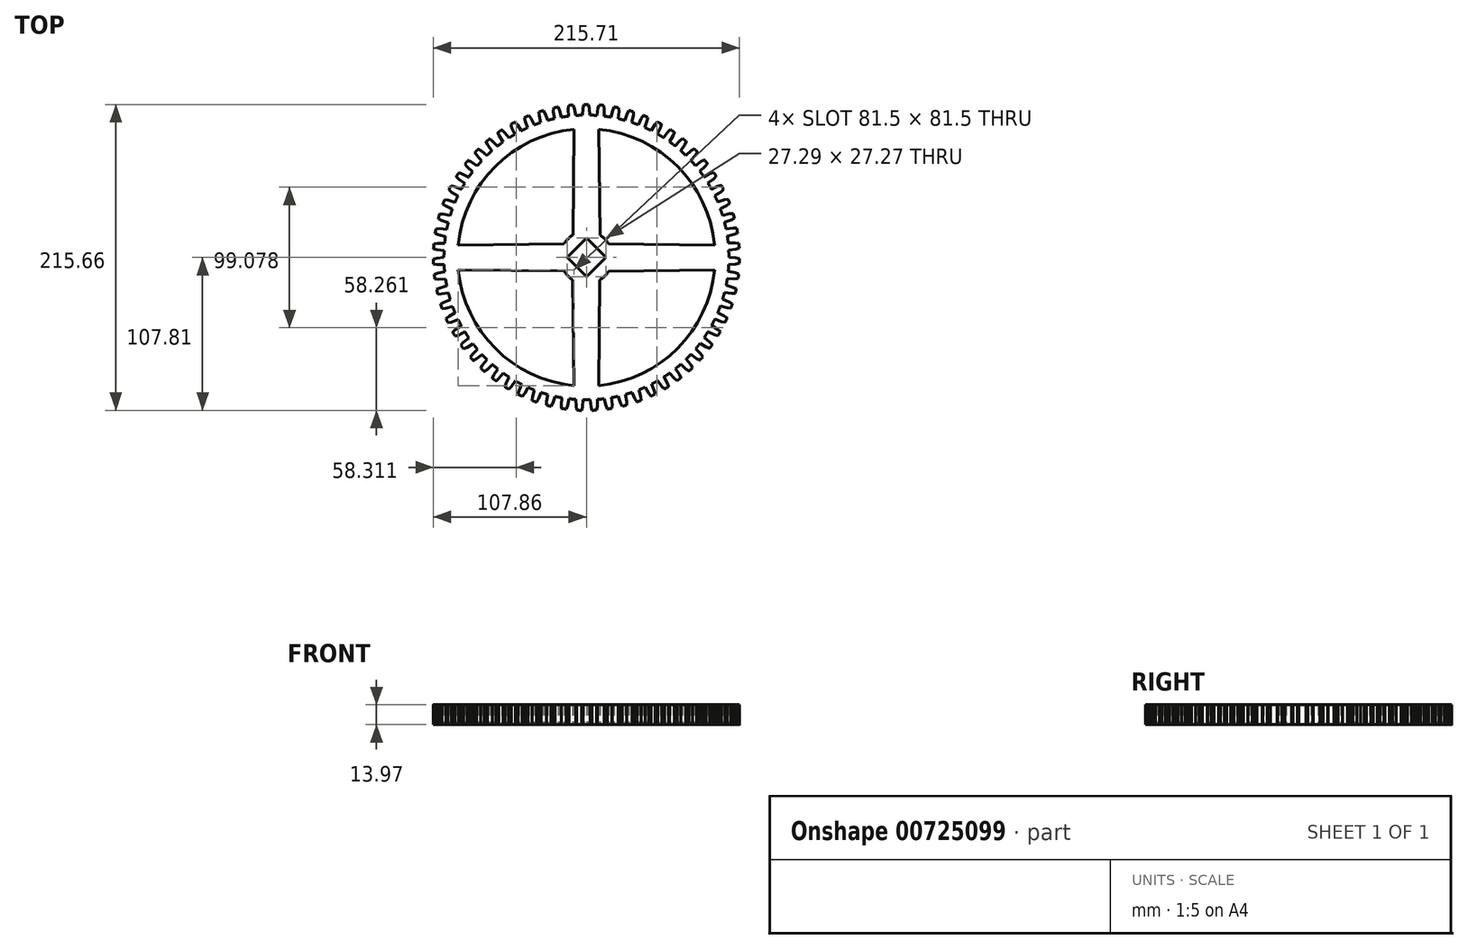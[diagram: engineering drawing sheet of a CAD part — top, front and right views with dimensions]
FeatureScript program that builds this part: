
annotation { "Feature Type Name" : "Feature", "Feature Type Description" : "" }
export const myFeature = defineFeature(function(context is Context, id is Id, definition is map)
    precondition{}
    {
        {
            var Q0;
            Q0=qCreatedBy(makeId("Top.planeOp"),FACE);
            var sketch = newSketch(context, id + "F0", { "sketchPlane" : qUnion([Q0])});
            skCircle(sketch, "E0", {"center": v(0, 0) * mm, "radius": 90.72 * mm});
            skCircle(sketch, "E1", {"center": v(0, 0) * mm, "radius": 107.86 * mm});
            skCircle(sketch, "E2", {"center": v(0, 0) * mm, "radius": 18.41 * mm});
            skLineSegment(sketch, "E3", {"start": v(0, 18.41) * mm, "end": v(0, 90.72) * mm});
            skLineSegment(sketch, "E4", {"start": v(18.41, 0) * mm, "end": v(90.72, 0) * mm});
            skLineSegment(sketch, "E5", {"start": v(-18.41, 0) * mm, "end": v(-90.72, 0) * mm});
            skLineSegment(sketch, "E6", {"start": v(0, -18.41) * mm, "end": v(0, -90.72) * mm});
            skLineSegment(sketch, "E7", {"start": v(9.72, 15.64) * mm, "end": v(8.79, 90.29) * mm});
            skLineSegment(sketch, "E8", {"start": v(-9.49, 15.78) * mm, "end": v(-8.79, 90.29) * mm});
            skLineSegment(sketch, "E9.1.0", {"start": v(-15.64, 9.72) * mm, "end": v(-90.29, 8.79) * mm});
            skLineSegment(sketch, "E9.1.1", {"start": v(-15.78, -9.49) * mm, "end": v(-90.29, -8.79) * mm});
            skLineSegment(sketch, "E9.2.0", {"start": v(-9.72, -15.64) * mm, "end": v(-8.79, -90.29) * mm});
            skLineSegment(sketch, "E9.2.1", {"start": v(9.49, -15.78) * mm, "end": v(8.79, -90.29) * mm});
            skLineSegment(sketch, "E9.3.0", {"start": v(15.64, -9.72) * mm, "end": v(90.29, -8.79) * mm});
            skLineSegment(sketch, "E9.3.1", {"start": v(15.78, 9.49) * mm, "end": v(90.29, 8.79) * mm});
            skLineSegment(sketch, "E10", {"start": v(0, 0) * mm, "end": v(0, -13.63) * mm});
            skLineSegment(sketch, "E11.bottom", {"start": v(127.17, 43.61) * mm, "end": v(146.45, 43.61) * mm});
            skLineSegment(sketch, "E11.top", {"start": v(127.17, 24.34) * mm, "end": v(146.45, 24.34) * mm});
            skLineSegment(sketch, "E11.left", {"start": v(127.17, 43.61) * mm, "end": v(127.17, 24.34) * mm});
            skLineSegment(sketch, "E11.right", {"start": v(146.45, 43.61) * mm, "end": v(146.45, 24.34) * mm});
            skLineSegment(sketch, "E12", {"start": v(0, -13.63) * mm, "end": v(-13.64, 0) * mm});
            skLineSegment(sketch, "E13", {"start": v(-13.64, 0) * mm, "end": v(0, 13.65) * mm});
            skLineSegment(sketch, "E14", {"start": v(0, 13.65) * mm, "end": v(13.66, 0) * mm});
            skLineSegment(sketch, "E15", {"start": v(13.66, 0) * mm, "end": v(0, -13.63) * mm});
            skLineSegment(sketch, "E16", {"start": v(0, 90.72) * mm, "end": v(-0.21, 107.86) * mm});
            skArc(sketch, "E17", {"start": v(-79.91, -60.73) * mm, "mid": v(84.25, 54.55) * mm, "end": v(-88.1, -48.07) * mm});
            skLineSegment(sketch, "E18", {"start": v(-0.18, 105.32) * mm, "end": v(-1.03, 105.31) * mm});
            skLineSegment(sketch, "E19", {"start": v(-0.18, 105.32) * mm, "end": v(2.05, 105.32) * mm});
            skLineSegment(sketch, "E20", {"start": v(2.42, 100.34) * mm, "end": v(2.05, 105.32) * mm});
            skLineSegment(sketch, "E21", {"start": v(1.44, 107.85) * mm, "end": v(2.05, 105.32) * mm});
            skLineSegment(sketch, "E22", {"start": v(-0.18, 105.32) * mm, "end": v(-2.42, 105.32) * mm});
            skLineSegment(sketch, "E23", {"start": v(-2.66, 100.33) * mm, "end": v(-2.42, 105.32) * mm});
            skLineSegment(sketch, "E24", {"start": v(-1.86, 107.84) * mm, "end": v(-2.42, 105.32) * mm});
            skLineSegment(sketch, "E25.1.0", {"start": v(-12.6, 107.12) * mm, "end": v(-12.9, 104.56) * mm});
            skLineSegment(sketch, "E25.1.1", {"start": v(-12.64, 99.57) * mm, "end": v(-12.9, 104.56) * mm});
            skLineSegment(sketch, "E25.1.2", {"start": v(-9.3, 107.46) * mm, "end": v(-8.44, 105) * mm});
            skLineSegment(sketch, "E25.1.3", {"start": v(-7.58, 100.08) * mm, "end": v(-8.44, 105) * mm});
            skLineSegment(sketch, "E25.2.0", {"start": v(-23.2, 105.34) * mm, "end": v(-23.24, 102.75) * mm});
            skLineSegment(sketch, "E25.2.1", {"start": v(-22.49, 97.82) * mm, "end": v(-23.24, 102.75) * mm});
            skLineSegment(sketch, "E25.2.2", {"start": v(-19.96, 106) * mm, "end": v(-18.86, 103.64) * mm});
            skLineSegment(sketch, "E25.2.3", {"start": v(-17.5, 98.83) * mm, "end": v(-18.86, 103.64) * mm});
            skLineSegment(sketch, "E25.3.0", {"start": v(-33.57, 102.5) * mm, "end": v(-33.35, 99.93) * mm});
            skLineSegment(sketch, "E25.3.1", {"start": v(-32.12, 95.1) * mm, "end": v(-33.35, 99.93) * mm});
            skLineSegment(sketch, "E25.3.2", {"start": v(-30.42, 103.48) * mm, "end": v(-29.08, 101.25) * mm});
            skLineSegment(sketch, "E25.3.3", {"start": v(-27.26, 96.6) * mm, "end": v(-29.08, 101.25) * mm});
            skLineSegment(sketch, "E25.4.0", {"start": v(-43.6, 98.65) * mm, "end": v(-43.14, 96.11) * mm});
            skLineSegment(sketch, "E25.4.1", {"start": v(-41.42, 91.42) * mm, "end": v(-43.14, 96.11) * mm});
            skLineSegment(sketch, "E25.4.2", {"start": v(-40.57, 99.94) * mm, "end": v(-39.02, 97.85) * mm});
            skLineSegment(sketch, "E25.4.3", {"start": v(-36.74, 93.4) * mm, "end": v(-39.02, 97.85) * mm});
            skLineSegment(sketch, "E25.5.0", {"start": v(-53.21, 93.82) * mm, "end": v(-52.5, 91.34) * mm});
            skLineSegment(sketch, "E25.5.1", {"start": v(-50.32, 86.84) * mm, "end": v(-52.5, 91.34) * mm});
            skLineSegment(sketch, "E25.5.2", {"start": v(-50.32, 95.4) * mm, "end": v(-48.57, 93.48) * mm});
            skLineSegment(sketch, "E25.5.3", {"start": v(-45.86, 89.28) * mm, "end": v(-48.57, 93.48) * mm});
            skLineSegment(sketch, "E25.6.0", {"start": v(-62.3, 88.06) * mm, "end": v(-61.33, 85.66) * mm});
            skLineSegment(sketch, "E25.6.1", {"start": v(-58.72, 81.4) * mm, "end": v(-61.33, 85.66) * mm});
            skLineSegment(sketch, "E25.6.2", {"start": v(-59.57, 89.92) * mm, "end": v(-57.63, 88.18) * mm});
            skLineSegment(sketch, "E25.6.3", {"start": v(-54.52, 84.27) * mm, "end": v(-57.63, 88.18) * mm});
            skLineSegment(sketch, "E25.7.0", {"start": v(-70.75, 81.42) * mm, "end": v(-69.55, 79.13) * mm});
            skLineSegment(sketch, "E25.7.1", {"start": v(-66.53, 75.15) * mm, "end": v(-69.55, 79.13) * mm});
            skLineSegment(sketch, "E25.7.2", {"start": v(-68.22, 83.54) * mm, "end": v(-66.13, 82) * mm});
            skLineSegment(sketch, "E25.7.3", {"start": v(-62.64, 78.42) * mm, "end": v(-66.13, 82) * mm});
            skLineSegment(sketch, "E25.8.0", {"start": v(-78.5, 73.97) * mm, "end": v(-77.08, 71.8) * mm});
            skLineSegment(sketch, "E25.8.1", {"start": v(-73.68, 68.15) * mm, "end": v(-77.08, 71.8) * mm});
            skLineSegment(sketch, "E25.8.2", {"start": v(-76.2, 76.34) * mm, "end": v(-73.96, 75) * mm});
            skLineSegment(sketch, "E25.8.3", {"start": v(-70.14, 71.8) * mm, "end": v(-73.96, 75) * mm});
            skLineSegment(sketch, "E25.9.0", {"start": v(-85.48, 65.78) * mm, "end": v(-83.85, 63.78) * mm});
            skLineSegment(sketch, "E25.9.1", {"start": v(-80.1, 60.48) * mm, "end": v(-83.85, 63.78) * mm});
            skLineSegment(sketch, "E25.9.2", {"start": v(-83.42, 68.37) * mm, "end": v(-81.06, 67.27) * mm});
            skLineSegment(sketch, "E25.9.3", {"start": v(-76.94, 64.45) * mm, "end": v(-81.06, 67.27) * mm});
            skLineSegment(sketch, "E25.10.0", {"start": v(-91.6, 56.95) * mm, "end": v(-89.78, 55.11) * mm});
            skLineSegment(sketch, "E25.10.1", {"start": v(-85.73, 52.2) * mm, "end": v(-89.78, 55.11) * mm});
            skLineSegment(sketch, "E25.10.2", {"start": v(-89.82, 59.72) * mm, "end": v(-87.36, 58.87) * mm});
            skLineSegment(sketch, "E25.10.3", {"start": v(-82.97, 56.47) * mm, "end": v(-87.36, 58.87) * mm});
            skLineSegment(sketch, "E25.11.0", {"start": v(-96.82, 47.54) * mm, "end": v(-94.82, 45.9) * mm});
            skLineSegment(sketch, "E25.11.1", {"start": v(-90.5, 43.4) * mm, "end": v(-94.82, 45.9) * mm});
            skLineSegment(sketch, "E25.11.2", {"start": v(-95.32, 50.48) * mm, "end": v(-92.79, 49.88) * mm});
            skLineSegment(sketch, "E25.11.3", {"start": v(-88.18, 47.93) * mm, "end": v(-92.79, 49.88) * mm});
            skLineSegment(sketch, "E25.12.0", {"start": v(-101.07, 37.67) * mm, "end": v(-98.92, 36.23) * mm});
            skLineSegment(sketch, "E25.12.1", {"start": v(-94.37, 34.18) * mm, "end": v(-98.92, 36.23) * mm});
            skLineSegment(sketch, "E25.12.2", {"start": v(-99.87, 40.74) * mm, "end": v(-97.3, 40.4) * mm});
            skLineSegment(sketch, "E25.12.3", {"start": v(-92.52, 38.91) * mm, "end": v(-97.3, 40.4) * mm});
            skLineSegment(sketch, "E25.13.0", {"start": v(-104.32, 27.41) * mm, "end": v(-102.04, 26.2) * mm});
            skLineSegment(sketch, "E25.13.1", {"start": v(-97.3, 24.61) * mm, "end": v(-102.04, 26.2) * mm});
            skLineSegment(sketch, "E25.13.2", {"start": v(-103.43, 30.6) * mm, "end": v(-100.83, 30.5) * mm});
            skLineSegment(sketch, "E25.13.3", {"start": v(-95.93, 29.5) * mm, "end": v(-100.83, 30.5) * mm});
            skLineSegment(sketch, "E25.14.0", {"start": v(-106.53, 16.9) * mm, "end": v(-104.14, 15.9) * mm});
            skLineSegment(sketch, "E25.14.1", {"start": v(-99.27, 14.8) * mm, "end": v(-104.14, 15.9) * mm});
            skLineSegment(sketch, "E25.14.2", {"start": v(-105.96, 20.14) * mm, "end": v(-103.36, 20.31) * mm});
            skLineSegment(sketch, "E25.14.3", {"start": v(-98.4, 19.8) * mm, "end": v(-103.36, 20.31) * mm});
            skLineSegment(sketch, "E25.15.0", {"start": v(-107.68, 6.2) * mm, "end": v(-105.2, 5.46) * mm});
            skLineSegment(sketch, "E25.15.1", {"start": v(-100.25, 4.85) * mm, "end": v(-105.2, 5.46) * mm});
            skLineSegment(sketch, "E25.15.2", {"start": v(-107.44, 9.5) * mm, "end": v(-104.87, 9.92) * mm});
            skLineSegment(sketch, "E25.15.3", {"start": v(-99.88, 9.91) * mm, "end": v(-104.87, 9.92) * mm});
            skLineSegment(sketch, "E25.16.0", {"start": v(-107.77, -4.55) * mm, "end": v(-105.23, -5.04) * mm});
            skLineSegment(sketch, "E25.16.1", {"start": v(-100.24, -5.16) * mm, "end": v(-105.23, -5.04) * mm});
            skLineSegment(sketch, "E25.16.2", {"start": v(-107.85, -1.25) * mm, "end": v(-105.34, -0.57) * mm});
            skLineSegment(sketch, "E25.16.3", {"start": v(-100.37, -0.08) * mm, "end": v(-105.34, -0.57) * mm});
            skLineSegment(sketch, "E25.17.0", {"start": v(-106.78, -15.26) * mm, "end": v(-104.2, -15.5) * mm});
            skLineSegment(sketch, "E25.17.1", {"start": v(-99.22, -15.11) * mm, "end": v(-104.2, -15.5) * mm});
            skLineSegment(sketch, "E25.17.2", {"start": v(-107.2, -11.98) * mm, "end": v(-104.76, -11.06) * mm});
            skLineSegment(sketch, "E25.17.3", {"start": v(-99.86, -10.07) * mm, "end": v(-104.76, -11.06) * mm});
            skLineSegment(sketch, "E25.18.0", {"start": v(-104.73, -25.81) * mm, "end": v(-102.14, -25.8) * mm});
            skLineSegment(sketch, "E25.18.1", {"start": v(-97.23, -24.92) * mm, "end": v(-102.14, -25.8) * mm});
            skLineSegment(sketch, "E25.18.2", {"start": v(-105.47, -22.6) * mm, "end": v(-103.14, -21.43) * mm});
            skLineSegment(sketch, "E25.18.3", {"start": v(-98.36, -19.97) * mm, "end": v(-103.14, -21.43) * mm});
            skLineSegment(sketch, "E25.19.0", {"start": v(-101.64, -36.11) * mm, "end": v(-99.07, -35.83) * mm});
            skLineSegment(sketch, "E25.19.1", {"start": v(-94.26, -34.48) * mm, "end": v(-99.07, -35.83) * mm});
            skLineSegment(sketch, "E25.19.2", {"start": v(-102.7, -32.99) * mm, "end": v(-100.5, -31.6) * mm});
            skLineSegment(sketch, "E25.19.3", {"start": v(-95.88, -29.66) * mm, "end": v(-100.5, -31.6) * mm});
            skLineSegment(sketch, "E25.20.0", {"start": v(-97.53, -46.05) * mm, "end": v(-95, -45.52) * mm});
            skLineSegment(sketch, "E25.20.1", {"start": v(-90.36, -43.69) * mm, "end": v(-95, -45.52) * mm});
            skLineSegment(sketch, "E25.20.2", {"start": v(-98.9, -43.05) * mm, "end": v(-96.85, -41.44) * mm});
            skLineSegment(sketch, "E25.20.3", {"start": v(-92.46, -39.06) * mm, "end": v(-96.85, -41.44) * mm});
            skLineSegment(sketch, "E25.21.0", {"start": v(-92.46, -55.54) * mm, "end": v(-90, -54.75) * mm});
            skLineSegment(sketch, "E25.21.1", {"start": v(-85.56, -52.47) * mm, "end": v(-90, -54.75) * mm});
            skLineSegment(sketch, "E25.21.2", {"start": v(-94.12, -52.68) * mm, "end": v(-92.24, -50.88) * mm});
            skLineSegment(sketch, "E25.21.3", {"start": v(-88.1, -48.07) * mm, "end": v(-92.24, -50.88) * mm});
            skLineSegment(sketch, "E25.22.0", {"start": v(-86.48, -64.47) * mm, "end": v(-84.1, -63.44) * mm});
            skLineSegment(sketch, "E25.22.1", {"start": v(-79.91, -60.73) * mm, "end": v(-84.1, -63.44) * mm});
            skLineSegment(sketch, "E25.22.2", {"start": v(-88.4, -61.79) * mm, "end": v(-86.71, -59.81) * mm});
            skLineSegment(sketch, "E25.22.3", {"start": v(-82.88, -56.6) * mm, "end": v(-86.71, -59.81) * mm});
            skLineSegment(sketch, "E25.23.0", {"start": v(-79.63, -72.76) * mm, "end": v(-77.37, -71.5) * mm});
            skLineSegment(sketch, "E25.23.1", {"start": v(-73.47, -68.38) * mm, "end": v(-77.37, -71.5) * mm});
            skLineSegment(sketch, "E25.23.2", {"start": v(-81.82, -70.29) * mm, "end": v(-80.33, -68.15) * mm});
            skLineSegment(sketch, "E25.23.3", {"start": v(-76.83, -64.58) * mm, "end": v(-80.33, -68.15) * mm});
            skLineSegment(sketch, "E25.24.0", {"start": v(-71.99, -80.32) * mm, "end": v(-69.87, -78.85) * mm});
            skLineSegment(sketch, "E25.24.1", {"start": v(-66.3, -75.36) * mm, "end": v(-69.87, -78.85) * mm});
            skLineSegment(sketch, "E25.24.2", {"start": v(-74.41, -78.08) * mm, "end": v(-73.14, -75.8) * mm});
            skLineSegment(sketch, "E25.24.3", {"start": v(-70.02, -71.9) * mm, "end": v(-73.14, -75.8) * mm});
            skLineSegment(sketch, "E25.25.0", {"start": v(-63.63, -87.1) * mm, "end": v(-61.67, -85.41) * mm});
            skLineSegment(sketch, "E25.25.1", {"start": v(-58.46, -81.58) * mm, "end": v(-61.67, -85.41) * mm});
            skLineSegment(sketch, "E25.25.2", {"start": v(-66.27, -85.1) * mm, "end": v(-65.23, -82.71) * mm});
            skLineSegment(sketch, "E25.25.3", {"start": v(-62.51, -78.52) * mm, "end": v(-65.23, -82.71) * mm});
            skLineSegment(sketch, "E25.26.0", {"start": v(-54.64, -93) * mm, "end": v(-52.86, -91.13) * mm});
            skLineSegment(sketch, "E25.26.1", {"start": v(-50.05, -87) * mm, "end": v(-52.86, -91.13) * mm});
            skLineSegment(sketch, "E25.26.2", {"start": v(-57.46, -91.28) * mm, "end": v(-56.67, -88.8) * mm});
            skLineSegment(sketch, "E25.26.3", {"start": v(-54.39, -84.36) * mm, "end": v(-56.67, -88.8) * mm});
            skLineSegment(sketch, "E25.27.0", {"start": v(-45.11, -97.97) * mm, "end": v(-43.52, -95.94) * mm});
            skLineSegment(sketch, "E25.27.1", {"start": v(-41.14, -91.55) * mm, "end": v(-43.52, -95.94) * mm});
            skLineSegment(sketch, "E25.27.2", {"start": v(-48.1, -96.55) * mm, "end": v(-47.55, -94) * mm});
            skLineSegment(sketch, "E25.27.3", {"start": v(-45.72, -89.35) * mm, "end": v(-47.55, -94) * mm});
            skLineSegment(sketch, "E25.28.0", {"start": v(-35.13, -101.98) * mm, "end": v(-33.75, -99.8) * mm});
            skLineSegment(sketch, "E25.28.1", {"start": v(-31.82, -95.2) * mm, "end": v(-33.75, -99.8) * mm});
            skLineSegment(sketch, "E25.28.2", {"start": v(-38.24, -100.86) * mm, "end": v(-37.95, -98.27) * mm});
            skLineSegment(sketch, "E25.28.3", {"start": v(-36.6, -93.46) * mm, "end": v(-37.95, -98.27) * mm});
            skLineSegment(sketch, "E25.29.0", {"start": v(-24.8, -104.97) * mm, "end": v(-23.65, -102.66) * mm});
            skLineSegment(sketch, "E25.29.1", {"start": v(-22.18, -97.89) * mm, "end": v(-23.65, -102.66) * mm});
            skLineSegment(sketch, "E25.29.2", {"start": v(-28, -104.16) * mm, "end": v(-27.98, -101.56) * mm});
            skLineSegment(sketch, "E25.29.3", {"start": v(-27.1, -96.64) * mm, "end": v(-27.98, -101.56) * mm});
            skLineSegment(sketch, "E25.30.0", {"start": v(-14.23, -106.92) * mm, "end": v(-13.3, -104.5) * mm});
            skLineSegment(sketch, "E25.30.1", {"start": v(-12.32, -99.6) * mm, "end": v(-13.3, -104.5) * mm});
            skLineSegment(sketch, "E25.30.2", {"start": v(-17.5, -106.43) * mm, "end": v(-17.73, -103.84) * mm});
            skLineSegment(sketch, "E25.30.3", {"start": v(-17.35, -98.86) * mm, "end": v(-17.73, -103.84) * mm});
            skLineSegment(sketch, "E25.31.0", {"start": v(-3.51, -107.8) * mm, "end": v(-2.84, -105.31) * mm});
            skLineSegment(sketch, "E25.31.1", {"start": v(-2.34, -100.34) * mm, "end": v(-2.84, -105.31) * mm});
            skLineSegment(sketch, "E25.31.2", {"start": v(-6.81, -107.65) * mm, "end": v(-7.3, -105.09) * mm});
            skLineSegment(sketch, "E25.31.3", {"start": v(-7.42, -100.1) * mm, "end": v(-7.3, -105.09) * mm});
            skLineSegment(sketch, "E25.32.0", {"start": v(7.24, -107.62) * mm, "end": v(7.66, -105.07) * mm});
            skLineSegment(sketch, "E25.32.1", {"start": v(7.66, -100.08) * mm, "end": v(7.66, -105.07) * mm});
            skLineSegment(sketch, "E25.32.2", {"start": v(3.94, -107.79) * mm, "end": v(3.2, -105.3) * mm});
            skLineSegment(sketch, "E25.32.3", {"start": v(2.58, -100.33) * mm, "end": v(3.2, -105.3) * mm});
            skLineSegment(sketch, "E25.33.0", {"start": v(17.92, -106.36) * mm, "end": v(18.09, -103.78) * mm});
            skLineSegment(sketch, "E25.33.1", {"start": v(17.58, -98.82) * mm, "end": v(18.09, -103.78) * mm});
            skLineSegment(sketch, "E25.33.2", {"start": v(14.65, -106.86) * mm, "end": v(13.67, -104.45) * mm});
            skLineSegment(sketch, "E25.33.3", {"start": v(12.56, -99.58) * mm, "end": v(13.67, -104.45) * mm});
            skLineSegment(sketch, "E25.34.0", {"start": v(28.42, -104.05) * mm, "end": v(28.33, -101.47) * mm});
            skLineSegment(sketch, "E25.34.1", {"start": v(27.34, -96.57) * mm, "end": v(28.33, -101.47) * mm});
            skLineSegment(sketch, "E25.34.2", {"start": v(25.22, -104.87) * mm, "end": v(24, -102.57) * mm});
            skLineSegment(sketch, "E25.34.3", {"start": v(22.41, -97.83) * mm, "end": v(24, -102.57) * mm});
            skLineSegment(sketch, "E25.35.0", {"start": v(38.64, -100.7) * mm, "end": v(38.3, -98.14) * mm});
            skLineSegment(sketch, "E25.35.1", {"start": v(36.82, -93.37) * mm, "end": v(38.3, -98.14) * mm});
            skLineSegment(sketch, "E25.35.2", {"start": v(35.54, -101.84) * mm, "end": v(34.1, -99.67) * mm});
            skLineSegment(sketch, "E25.35.3", {"start": v(32.04, -95.12) * mm, "end": v(34.1, -99.67) * mm});
            skLineSegment(sketch, "E25.36.0", {"start": v(48.47, -96.36) * mm, "end": v(47.87, -93.84) * mm});
            skLineSegment(sketch, "E25.36.1", {"start": v(45.93, -89.24) * mm, "end": v(47.87, -93.84) * mm});
            skLineSegment(sketch, "E25.36.2", {"start": v(45.5, -97.8) * mm, "end": v(43.85, -95.78) * mm});
            skLineSegment(sketch, "E25.36.3", {"start": v(41.35, -91.45) * mm, "end": v(43.85, -95.78) * mm});
            skLineSegment(sketch, "E25.37.0", {"start": v(57.82, -91.05) * mm, "end": v(56.98, -88.6) * mm});
            skLineSegment(sketch, "E25.37.1", {"start": v(54.59, -84.23) * mm, "end": v(56.98, -88.6) * mm});
            skLineSegment(sketch, "E25.37.2", {"start": v(55.01, -92.78) * mm, "end": v(53.17, -90.94) * mm});
            skLineSegment(sketch, "E25.37.3", {"start": v(50.25, -86.88) * mm, "end": v(53.17, -90.94) * mm});
            skLineSegment(sketch, "E25.38.0", {"start": v(66.6, -84.84) * mm, "end": v(65.52, -82.5) * mm});
            skLineSegment(sketch, "E25.38.1", {"start": v(62.7, -78.37) * mm, "end": v(65.52, -82.5) * mm});
            skLineSegment(sketch, "E25.38.2", {"start": v(63.97, -86.84) * mm, "end": v(61.96, -85.2) * mm});
            skLineSegment(sketch, "E25.38.3", {"start": v(58.66, -81.45) * mm, "end": v(61.96, -85.2) * mm});
            skLineSegment(sketch, "E25.39.0", {"start": v(74.72, -77.79) * mm, "end": v(73.4, -75.56) * mm});
            skLineSegment(sketch, "E25.39.1", {"start": v(70.2, -71.74) * mm, "end": v(73.4, -75.56) * mm});
            skLineSegment(sketch, "E25.39.2", {"start": v(72.3, -80.04) * mm, "end": v(70.13, -78.6) * mm});
            skLineSegment(sketch, "E25.39.3", {"start": v(66.47, -75.2) * mm, "end": v(70.13, -78.6) * mm});
            skLineSegment(sketch, "E25.40.0", {"start": v(82.1, -69.96) * mm, "end": v(80.57, -67.88) * mm});
            skLineSegment(sketch, "E25.40.1", {"start": v(76.99, -64.4) * mm, "end": v(80.57, -67.88) * mm});
            skLineSegment(sketch, "E25.40.2", {"start": v(79.91, -72.44) * mm, "end": v(77.6, -71.23) * mm});
            skLineSegment(sketch, "E25.40.3", {"start": v(73.63, -68.2) * mm, "end": v(77.6, -71.23) * mm});
            skLineSegment(sketch, "E25.41.0", {"start": v(88.65, -61.44) * mm, "end": v(86.92, -59.52) * mm});
            skLineSegment(sketch, "E25.41.1", {"start": v(83.02, -56.4) * mm, "end": v(86.92, -59.52) * mm});
            skLineSegment(sketch, "E25.41.2", {"start": v(86.73, -64.13) * mm, "end": v(84.32, -63.15) * mm});
            skLineSegment(sketch, "E25.41.3", {"start": v(80.06, -60.54) * mm, "end": v(84.32, -63.15) * mm});
            skLineSegment(sketch, "E25.42.0", {"start": v(94.33, -52.3) * mm, "end": v(92.42, -50.57) * mm});
            skLineSegment(sketch, "E25.42.1", {"start": v(88.22, -47.86) * mm, "end": v(92.42, -50.57) * mm});
            skLineSegment(sketch, "E25.42.2", {"start": v(92.68, -55.17) * mm, "end": v(90.18, -54.44) * mm});
            skLineSegment(sketch, "E25.42.3", {"start": v(85.69, -52.27) * mm, "end": v(90.18, -54.44) * mm});
            skLineSegment(sketch, "E25.43.0", {"start": v(99.07, -42.66) * mm, "end": v(97, -41.11) * mm});
            skLineSegment(sketch, "E25.43.1", {"start": v(92.55, -38.84) * mm, "end": v(97, -41.11) * mm});
            skLineSegment(sketch, "E25.43.2", {"start": v(97.72, -45.67) * mm, "end": v(95.16, -45.19) * mm});
            skLineSegment(sketch, "E25.43.3", {"start": v(90.46, -43.47) * mm, "end": v(95.16, -45.19) * mm});
            skLineSegment(sketch, "E25.44.0", {"start": v(102.82, -32.58) * mm, "end": v(100.6, -31.25) * mm});
            skLineSegment(sketch, "E25.44.1", {"start": v(95.96, -29.43) * mm, "end": v(100.6, -31.25) * mm});
            skLineSegment(sketch, "E25.44.2", {"start": v(101.78, -35.71) * mm, "end": v(99.18, -35.5) * mm});
            skLineSegment(sketch, "E25.44.3", {"start": v(94.34, -34.25) * mm, "end": v(99.18, -35.5) * mm});
            skLineSegment(sketch, "E25.45.0", {"start": v(105.56, -22.18) * mm, "end": v(103.22, -21.08) * mm});
            skLineSegment(sketch, "E25.45.1", {"start": v(98.4, -19.73) * mm, "end": v(103.22, -21.08) * mm});
            skLineSegment(sketch, "E25.45.2", {"start": v(104.83, -25.4) * mm, "end": v(102.22, -25.44) * mm});
            skLineSegment(sketch, "E25.45.3", {"start": v(97.28, -24.69) * mm, "end": v(102.22, -25.44) * mm});
            skLineSegment(sketch, "E25.46.0", {"start": v(107.24, -11.56) * mm, "end": v(104.8, -10.7) * mm});
            skLineSegment(sketch, "E25.46.1", {"start": v(99.88, -9.84) * mm, "end": v(104.8, -10.7) * mm});
            skLineSegment(sketch, "E25.46.2", {"start": v(106.84, -14.84) * mm, "end": v(104.25, -15.13) * mm});
            skLineSegment(sketch, "E25.46.3", {"start": v(99.26, -14.88) * mm, "end": v(104.25, -15.13) * mm});
            skLineSegment(sketch, "E25.47.0", {"start": v(107.86, -0.83) * mm, "end": v(105.35, -0.2) * mm});
            skLineSegment(sketch, "E25.47.1", {"start": v(100.37, 0.16) * mm, "end": v(105.35, -0.2) * mm});
            skLineSegment(sketch, "E25.47.2", {"start": v(107.78, -4.13) * mm, "end": v(105.24, -4.68) * mm});
            skLineSegment(sketch, "E25.47.3", {"start": v(100.25, -4.92) * mm, "end": v(105.24, -4.68) * mm});
            skLineSegment(sketch, "E25.48.0", {"start": v(107.4, 9.92) * mm, "end": v(104.85, 10.28) * mm});
            skLineSegment(sketch, "E25.48.1", {"start": v(99.85, 10.15) * mm, "end": v(104.85, 10.28) * mm});
            skLineSegment(sketch, "E25.48.2", {"start": v(107.66, 6.63) * mm, "end": v(105.18, 5.82) * mm});
            skLineSegment(sketch, "E25.48.3", {"start": v(100.24, 5.08) * mm, "end": v(105.18, 5.82) * mm});
            skLineSegment(sketch, "E25.49.0", {"start": v(105.88, 20.56) * mm, "end": v(103.3, 20.67) * mm});
            skLineSegment(sketch, "E25.49.1", {"start": v(98.35, 20.04) * mm, "end": v(103.3, 20.67) * mm});
            skLineSegment(sketch, "E25.49.2", {"start": v(106.46, 17.31) * mm, "end": v(104.08, 16.27) * mm});
            skLineSegment(sketch, "E25.49.3", {"start": v(99.23, 15.04) * mm, "end": v(104.08, 16.27) * mm});
            skLineSegment(sketch, "E25.50.0", {"start": v(103.3, 31) * mm, "end": v(100.73, 30.85) * mm});
            skLineSegment(sketch, "E25.50.1", {"start": v(95.86, 29.73) * mm, "end": v(100.73, 30.85) * mm});
            skLineSegment(sketch, "E25.50.2", {"start": v(104.21, 27.83) * mm, "end": v(101.94, 26.55) * mm});
            skLineSegment(sketch, "E25.50.3", {"start": v(97.24, 24.85) * mm, "end": v(101.94, 26.55) * mm});
            skLineSegment(sketch, "E25.51.0", {"start": v(99.7, 41.14) * mm, "end": v(97.16, 40.73) * mm});
            skLineSegment(sketch, "E25.51.1", {"start": v(92.43, 39.13) * mm, "end": v(97.16, 40.73) * mm});
            skLineSegment(sketch, "E25.51.2", {"start": v(100.92, 38.06) * mm, "end": v(98.8, 36.57) * mm});
            skLineSegment(sketch, "E25.51.3", {"start": v(94.29, 34.4) * mm, "end": v(98.8, 36.57) * mm});
            skLineSegment(sketch, "E25.52.0", {"start": v(95.12, 50.86) * mm, "end": v(92.62, 50.2) * mm});
            skLineSegment(sketch, "E25.52.1", {"start": v(88.07, 48.14) * mm, "end": v(92.62, 50.2) * mm});
            skLineSegment(sketch, "E25.52.2", {"start": v(96.63, 47.92) * mm, "end": v(94.66, 46.22) * mm});
            skLineSegment(sketch, "E25.52.3", {"start": v(90.4, 43.62) * mm, "end": v(94.66, 46.22) * mm});
            skLineSegment(sketch, "E25.53.0", {"start": v(89.58, 60.08) * mm, "end": v(87.16, 59.17) * mm});
            skLineSegment(sketch, "E25.53.1", {"start": v(82.84, 56.67) * mm, "end": v(87.16, 59.17) * mm});
            skLineSegment(sketch, "E25.53.2", {"start": v(91.38, 57.3) * mm, "end": v(89.59, 55.42) * mm});
            skLineSegment(sketch, "E25.53.3", {"start": v(85.6, 52.4) * mm, "end": v(89.59, 55.42) * mm});
            skLineSegment(sketch, "E25.54.0", {"start": v(83.15, 68.7) * mm, "end": v(80.84, 67.56) * mm});
            skLineSegment(sketch, "E25.54.1", {"start": v(76.79, 64.64) * mm, "end": v(80.84, 67.56) * mm});
            skLineSegment(sketch, "E25.54.2", {"start": v(85.22, 66.12) * mm, "end": v(83.62, 64.06) * mm});
            skLineSegment(sketch, "E25.54.3", {"start": v(79.96, 60.67) * mm, "end": v(83.62, 64.06) * mm});
            skLineSegment(sketch, "E25.55.0", {"start": v(75.9, 76.64) * mm, "end": v(73.7, 75.27) * mm});
            skLineSegment(sketch, "E25.55.1", {"start": v(69.97, 71.96) * mm, "end": v(73.7, 75.27) * mm});
            skLineSegment(sketch, "E25.55.2", {"start": v(78.21, 74.28) * mm, "end": v(76.83, 72.07) * mm});
            skLineSegment(sketch, "E25.55.3", {"start": v(73.52, 68.33) * mm, "end": v(76.83, 72.07) * mm});
            skLineSegment(sketch, "E25.56.0", {"start": v(67.9, 83.81) * mm, "end": v(65.85, 82.23) * mm});
            skLineSegment(sketch, "E25.56.1", {"start": v(62.46, 78.57) * mm, "end": v(65.85, 82.23) * mm});
            skLineSegment(sketch, "E25.56.2", {"start": v(70.43, 81.7) * mm, "end": v(69.27, 79.36) * mm});
            skLineSegment(sketch, "E25.56.3", {"start": v(66.35, 75.3) * mm, "end": v(69.27, 79.36) * mm});
            skLineSegment(sketch, "E25.57.0", {"start": v(59.21, 90.16) * mm, "end": v(57.33, 88.38) * mm});
            skLineSegment(sketch, "E25.57.1", {"start": v(54.32, 84.4) * mm, "end": v(57.33, 88.38) * mm});
            skLineSegment(sketch, "E25.57.2", {"start": v(61.94, 88.3) * mm, "end": v(61.03, 85.86) * mm});
            skLineSegment(sketch, "E25.57.3", {"start": v(58.52, 81.54) * mm, "end": v(61.03, 85.86) * mm});
            skLineSegment(sketch, "E25.58.0", {"start": v(49.94, 95.6) * mm, "end": v(48.25, 93.65) * mm});
            skLineSegment(sketch, "E25.58.1", {"start": v(45.65, 89.39) * mm, "end": v(48.25, 93.65) * mm});
            skLineSegment(sketch, "E25.58.2", {"start": v(52.84, 94.03) * mm, "end": v(52.17, 91.51) * mm});
            skLineSegment(sketch, "E25.58.3", {"start": v(50.11, 86.96) * mm, "end": v(52.17, 91.51) * mm});
            skLineSegment(sketch, "E25.59.0", {"start": v(40.17, 100.1) * mm, "end": v(38.68, 97.99) * mm});
            skLineSegment(sketch, "E25.59.1", {"start": v(36.52, 93.49) * mm, "end": v(38.68, 97.99) * mm});
            skLineSegment(sketch, "E25.59.2", {"start": v(43.22, 98.82) * mm, "end": v(42.8, 96.25) * mm});
            skLineSegment(sketch, "E25.59.3", {"start": v(41.2, 91.52) * mm, "end": v(42.8, 96.25) * mm});
            skLineSegment(sketch, "E25.60.0", {"start": v(30, 103.6) * mm, "end": v(28.73, 101.35) * mm});
            skLineSegment(sketch, "E25.60.1", {"start": v(27.03, 96.66) * mm, "end": v(28.73, 101.35) * mm});
            skLineSegment(sketch, "E25.60.2", {"start": v(33.16, 102.64) * mm, "end": v(33, 100.04) * mm});
            skLineSegment(sketch, "E25.60.3", {"start": v(31.89, 95.17) * mm, "end": v(33, 100.04) * mm});
            skLineSegment(sketch, "E25.61.0", {"start": v(19.54, 106.08) * mm, "end": v(18.5, 103.71) * mm});
            skLineSegment(sketch, "E25.61.1", {"start": v(17.27, 98.87) * mm, "end": v(18.5, 103.71) * mm});
            skLineSegment(sketch, "E25.61.2", {"start": v(22.78, 105.43) * mm, "end": v(22.88, 102.83) * mm});
            skLineSegment(sketch, "E25.61.3", {"start": v(22.25, 97.87) * mm, "end": v(22.88, 102.83) * mm});
            skLineSegment(sketch, "E25.62.0", {"start": v(8.88, 107.5) * mm, "end": v(8.08, 105.04) * mm});
            skLineSegment(sketch, "E25.62.1", {"start": v(7.34, 100.1) * mm, "end": v(8.08, 105.04) * mm});
            skLineSegment(sketch, "E25.62.2", {"start": v(12.17, 107.17) * mm, "end": v(12.53, 104.6) * mm});
            skLineSegment(sketch, "E25.62.3", {"start": v(12.4, 99.6) * mm, "end": v(12.53, 104.6) * mm});
            skArc(sketch, "E26.trimOffspring", {"start": v(-85.56, -52.47) * mm, "mid": v(-84.25, -54.55) * mm, "end": v(-82.88, -56.6) * mm});
            skSolve(sketch);
        }
        {
            var Q0;
            {var subQ94=sQuery(id+"F0.wireOp",EDGE,"E25.21.0");Q0=makeQuery(id+"F0.imprint","IMPRINT",FACE,{"disambiguationData":[TD([[makeQuery(id+"F0.imprint","IMPRINT",EDGE,{"derivedFrom":subQ94}),1.0]])]});}
            var Q1;
            {var subQ0=sQuery(id+"F0.wireOp",EDGE,"E3");Q1=makeQuery(id+"F0.imprint","IMPRINT",FACE,{"disambiguationData":[TD([[makeQuery(id+"F0.imprint","IMPRINT",EDGE,{"derivedFrom":subQ0}),1.0]])]});}
            var Q2;
            {var subQ0=sQuery(id+"F0.wireOp",EDGE,"E5");Q2=makeQuery(id+"F0.imprint","IMPRINT",FACE,{"disambiguationData":[TD([[makeQuery(id+"F0.imprint","IMPRINT",EDGE,{"derivedFrom":subQ0}),-1.0]])]});}
            var Q3;
            {var subQ0=sQuery(id+"F0.wireOp",EDGE,"E5");Q3=makeQuery(id+"F0.imprint","IMPRINT",FACE,{"disambiguationData":[TD([[makeQuery(id+"F0.imprint","IMPRINT",EDGE,{"derivedFrom":subQ0}),1.0]])]});}
            var Q4;
            {var subQ0=sQuery(id+"F0.wireOp",EDGE,"E6");Q4=makeQuery(id+"F0.imprint","IMPRINT",FACE,{"disambiguationData":[TD([[makeQuery(id+"F0.imprint","IMPRINT",EDGE,{"derivedFrom":subQ0}),-1.0]])]});}
            var Q5;
            {var subQ0=sQuery(id+"F0.wireOp",EDGE,"E6");Q5=makeQuery(id+"F0.imprint","IMPRINT",FACE,{"disambiguationData":[TD([[makeQuery(id+"F0.imprint","IMPRINT",EDGE,{"derivedFrom":subQ0}),1.0]])]});}
            var Q6;
            {var subQ0=sQuery(id+"F0.wireOp",EDGE,"E4");Q6=makeQuery(id+"F0.imprint","IMPRINT",FACE,{"disambiguationData":[TD([[makeQuery(id+"F0.imprint","IMPRINT",EDGE,{"derivedFrom":subQ0}),-1.0]])]});}
            var Q7;
            {var subQ0=sQuery(id+"F0.wireOp",EDGE,"E4");Q7=makeQuery(id+"F0.imprint","IMPRINT",FACE,{"disambiguationData":[TD([[makeQuery(id+"F0.imprint","IMPRINT",EDGE,{"derivedFrom":subQ0}),1.0]])]});}
            var Q8;
            Q8=makeQuery(id+"F0.imprint","IMPRINT",FACE,{"disambiguationData":[TD([[makeQuery(id+"F0.imprint","IMPRINT",EDGE,{"derivedFrom":sQuery(id+"F0.wireOp",EDGE,"E12")}),1.0]])]});
            var Q9;
            {var subQ1=sQuery(id+"F0.wireOp",EDGE,"E25.62.0");Q9=makeQuery(id+"F0.imprint","IMPRINT",FACE,{"disambiguationData":[TD([[makeQuery(id+"F0.imprint","IMPRINT",EDGE,{"derivedFrom":subQ1}),1.0]])]});}
            var Q10;
            {var subQ1=sQuery(id+"F0.wireOp",EDGE,"E25.61.0");Q10=makeQuery(id+"F0.imprint","IMPRINT",FACE,{"disambiguationData":[TD([[makeQuery(id+"F0.imprint","IMPRINT",EDGE,{"derivedFrom":subQ1}),1.0]])]});}
            var Q11;
            {var subQ1=sQuery(id+"F0.wireOp",EDGE,"E25.60.0");Q11=makeQuery(id+"F0.imprint","IMPRINT",FACE,{"disambiguationData":[TD([[makeQuery(id+"F0.imprint","IMPRINT",EDGE,{"derivedFrom":subQ1}),1.0]])]});}
            var Q12;
            {var subQ0=sQuery(id+"F0.wireOp",EDGE,"E25.59.0");Q12=makeQuery(id+"F0.imprint","IMPRINT",FACE,{"disambiguationData":[TD([[makeQuery(id+"F0.imprint","IMPRINT",EDGE,{"derivedFrom":subQ0}),1.0]])]});}
            var Q13;
            {var subQ0=sQuery(id+"F0.wireOp",EDGE,"E25.58.0");Q13=makeQuery(id+"F0.imprint","IMPRINT",FACE,{"disambiguationData":[TD([[makeQuery(id+"F0.imprint","IMPRINT",EDGE,{"derivedFrom":subQ0}),1.0]])]});}
            var Q14;
            {var subQ3=sQuery(id+"F0.wireOp",EDGE,"E25.57.0");Q14=makeQuery(id+"F0.imprint","IMPRINT",FACE,{"disambiguationData":[TD([[makeQuery(id+"F0.imprint","IMPRINT",EDGE,{"derivedFrom":subQ3}),1.0]])]});}
            var Q15;
            {var subQ3=sQuery(id+"F0.wireOp",EDGE,"E25.56.0");Q15=makeQuery(id+"F0.imprint","IMPRINT",FACE,{"disambiguationData":[TD([[makeQuery(id+"F0.imprint","IMPRINT",EDGE,{"derivedFrom":subQ3}),1.0]])]});}
            var Q16;
            {var subQ1=sQuery(id+"F0.wireOp",EDGE,"E25.55.0");Q16=makeQuery(id+"F0.imprint","IMPRINT",FACE,{"disambiguationData":[TD([[makeQuery(id+"F0.imprint","IMPRINT",EDGE,{"derivedFrom":subQ1}),1.0]])]});}
            var Q17;
            {var subQ0=sQuery(id+"F0.wireOp",EDGE,"E25.54.0");Q17=makeQuery(id+"F0.imprint","IMPRINT",FACE,{"disambiguationData":[TD([[makeQuery(id+"F0.imprint","IMPRINT",EDGE,{"derivedFrom":subQ0}),1.0]])]});}
            var Q18;
            {var subQ0=sQuery(id+"F0.wireOp",EDGE,"E25.53.0");Q18=makeQuery(id+"F0.imprint","IMPRINT",FACE,{"disambiguationData":[TD([[makeQuery(id+"F0.imprint","IMPRINT",EDGE,{"derivedFrom":subQ0}),1.0]])]});}
            var Q19;
            {var subQ1=sQuery(id+"F0.wireOp",EDGE,"E25.52.0");Q19=makeQuery(id+"F0.imprint","IMPRINT",FACE,{"disambiguationData":[TD([[makeQuery(id+"F0.imprint","IMPRINT",EDGE,{"derivedFrom":subQ1}),1.0]])]});}
            var Q20;
            {var subQ4=sQuery(id+"F0.wireOp",EDGE,"E25.51.0");Q20=makeQuery(id+"F0.imprint","IMPRINT",FACE,{"disambiguationData":[TD([[makeQuery(id+"F0.imprint","IMPRINT",EDGE,{"derivedFrom":subQ4}),1.0]])]});}
            var Q21;
            {var subQ1=sQuery(id+"F0.wireOp",EDGE,"E25.50.0");Q21=makeQuery(id+"F0.imprint","IMPRINT",FACE,{"disambiguationData":[TD([[makeQuery(id+"F0.imprint","IMPRINT",EDGE,{"derivedFrom":subQ1}),1.0]])]});}
            var Q22;
            {var subQ0=sQuery(id+"F0.wireOp",EDGE,"E25.49.0");Q22=makeQuery(id+"F0.imprint","IMPRINT",FACE,{"disambiguationData":[TD([[makeQuery(id+"F0.imprint","IMPRINT",EDGE,{"derivedFrom":subQ0}),1.0]])]});}
            var Q23;
            {var subQ0=sQuery(id+"F0.wireOp",EDGE,"E25.48.0");Q23=makeQuery(id+"F0.imprint","IMPRINT",FACE,{"disambiguationData":[TD([[makeQuery(id+"F0.imprint","IMPRINT",EDGE,{"derivedFrom":subQ0}),1.0]])]});}
            var Q24;
            {var subQ1=sQuery(id+"F0.wireOp",EDGE,"E25.47.0");Q24=makeQuery(id+"F0.imprint","IMPRINT",FACE,{"disambiguationData":[TD([[makeQuery(id+"F0.imprint","IMPRINT",EDGE,{"derivedFrom":subQ1}),1.0]])]});}
            var Q25;
            {var subQ3=sQuery(id+"F0.wireOp",EDGE,"E25.46.0");Q25=makeQuery(id+"F0.imprint","IMPRINT",FACE,{"disambiguationData":[TD([[makeQuery(id+"F0.imprint","IMPRINT",EDGE,{"derivedFrom":subQ3}),1.0]])]});}
            var Q26;
            {var subQ1=sQuery(id+"F0.wireOp",EDGE,"E25.45.0");Q26=makeQuery(id+"F0.imprint","IMPRINT",FACE,{"disambiguationData":[TD([[makeQuery(id+"F0.imprint","IMPRINT",EDGE,{"derivedFrom":subQ1}),1.0]])]});}
            var Q27;
            {var subQ0=sQuery(id+"F0.wireOp",EDGE,"E25.44.0");Q27=makeQuery(id+"F0.imprint","IMPRINT",FACE,{"disambiguationData":[TD([[makeQuery(id+"F0.imprint","IMPRINT",EDGE,{"derivedFrom":subQ0}),1.0]])]});}
            var Q28;
            {var subQ1=sQuery(id+"F0.wireOp",EDGE,"E25.43.0");Q28=makeQuery(id+"F0.imprint","IMPRINT",FACE,{"disambiguationData":[TD([[makeQuery(id+"F0.imprint","IMPRINT",EDGE,{"derivedFrom":subQ1}),1.0]])]});}
            var Q29;
            {var subQ1=sQuery(id+"F0.wireOp",EDGE,"E25.42.0");Q29=makeQuery(id+"F0.imprint","IMPRINT",FACE,{"disambiguationData":[TD([[makeQuery(id+"F0.imprint","IMPRINT",EDGE,{"derivedFrom":subQ1}),1.0]])]});}
            var Q30;
            {var subQ1=sQuery(id+"F0.wireOp",EDGE,"E25.41.0");Q30=makeQuery(id+"F0.imprint","IMPRINT",FACE,{"disambiguationData":[TD([[makeQuery(id+"F0.imprint","IMPRINT",EDGE,{"derivedFrom":subQ1}),1.0]])]});}
            var Q31;
            {var subQ1=sQuery(id+"F0.wireOp",EDGE,"E25.40.0");Q31=makeQuery(id+"F0.imprint","IMPRINT",FACE,{"disambiguationData":[TD([[makeQuery(id+"F0.imprint","IMPRINT",EDGE,{"derivedFrom":subQ1}),1.0]])]});}
            var Q32;
            {var subQ0=sQuery(id+"F0.wireOp",EDGE,"E25.39.0");Q32=makeQuery(id+"F0.imprint","IMPRINT",FACE,{"disambiguationData":[TD([[makeQuery(id+"F0.imprint","IMPRINT",EDGE,{"derivedFrom":subQ0}),1.0]])]});}
            var Q33;
            {var subQ1=sQuery(id+"F0.wireOp",EDGE,"E25.38.0");Q33=makeQuery(id+"F0.imprint","IMPRINT",FACE,{"disambiguationData":[TD([[makeQuery(id+"F0.imprint","IMPRINT",EDGE,{"derivedFrom":subQ1}),1.0]])]});}
            var Q34;
            {var subQ1=sQuery(id+"F0.wireOp",EDGE,"E25.37.0");Q34=makeQuery(id+"F0.imprint","IMPRINT",FACE,{"disambiguationData":[TD([[makeQuery(id+"F0.imprint","IMPRINT",EDGE,{"derivedFrom":subQ1}),1.0]])]});}
            var Q35;
            {var subQ1=sQuery(id+"F0.wireOp",EDGE,"E25.36.0");Q35=makeQuery(id+"F0.imprint","IMPRINT",FACE,{"disambiguationData":[TD([[makeQuery(id+"F0.imprint","IMPRINT",EDGE,{"derivedFrom":subQ1}),1.0]])]});}
            var Q36;
            {var subQ3=sQuery(id+"F0.wireOp",EDGE,"E25.35.0");Q36=makeQuery(id+"F0.imprint","IMPRINT",FACE,{"disambiguationData":[TD([[makeQuery(id+"F0.imprint","IMPRINT",EDGE,{"derivedFrom":subQ3}),1.0]])]});}
            var Q37;
            {var subQ0=sQuery(id+"F0.wireOp",EDGE,"E25.34.0");Q37=makeQuery(id+"F0.imprint","IMPRINT",FACE,{"disambiguationData":[TD([[makeQuery(id+"F0.imprint","IMPRINT",EDGE,{"derivedFrom":subQ0}),1.0]])]});}
            var Q38;
            {var subQ1=sQuery(id+"F0.wireOp",EDGE,"E25.33.0");Q38=makeQuery(id+"F0.imprint","IMPRINT",FACE,{"disambiguationData":[TD([[makeQuery(id+"F0.imprint","IMPRINT",EDGE,{"derivedFrom":subQ1}),1.0]])]});}
            var Q39;
            {var subQ1=sQuery(id+"F0.wireOp",EDGE,"E25.32.0");Q39=makeQuery(id+"F0.imprint","IMPRINT",FACE,{"disambiguationData":[TD([[makeQuery(id+"F0.imprint","IMPRINT",EDGE,{"derivedFrom":subQ1}),1.0]])]});}
            var Q40;
            {var subQ1=sQuery(id+"F0.wireOp",EDGE,"E25.31.0");Q40=makeQuery(id+"F0.imprint","IMPRINT",FACE,{"disambiguationData":[TD([[makeQuery(id+"F0.imprint","IMPRINT",EDGE,{"derivedFrom":subQ1}),1.0]])]});}
            var Q41;
            {var subQ1=sQuery(id+"F0.wireOp",EDGE,"E25.30.0");Q41=makeQuery(id+"F0.imprint","IMPRINT",FACE,{"disambiguationData":[TD([[makeQuery(id+"F0.imprint","IMPRINT",EDGE,{"derivedFrom":subQ1}),1.0]])]});}
            var Q42;
            {var subQ0=sQuery(id+"F0.wireOp",EDGE,"E25.29.0");Q42=makeQuery(id+"F0.imprint","IMPRINT",FACE,{"disambiguationData":[TD([[makeQuery(id+"F0.imprint","IMPRINT",EDGE,{"derivedFrom":subQ0}),1.0]])]});}
            var Q43;
            {var subQ1=sQuery(id+"F0.wireOp",EDGE,"E25.28.0");Q43=makeQuery(id+"F0.imprint","IMPRINT",FACE,{"disambiguationData":[TD([[makeQuery(id+"F0.imprint","IMPRINT",EDGE,{"derivedFrom":subQ1}),1.0]])]});}
            var Q44;
            {var subQ1=sQuery(id+"F0.wireOp",EDGE,"E25.27.0");Q44=makeQuery(id+"F0.imprint","IMPRINT",FACE,{"disambiguationData":[TD([[makeQuery(id+"F0.imprint","IMPRINT",EDGE,{"derivedFrom":subQ1}),1.0]])]});}
            var Q45;
            {var subQ1=sQuery(id+"F0.wireOp",EDGE,"E25.26.0");Q45=makeQuery(id+"F0.imprint","IMPRINT",FACE,{"disambiguationData":[TD([[makeQuery(id+"F0.imprint","IMPRINT",EDGE,{"derivedFrom":subQ1}),1.0]])]});}
            var Q46;
            {var subQ1=sQuery(id+"F0.wireOp",EDGE,"E25.25.0");Q46=makeQuery(id+"F0.imprint","IMPRINT",FACE,{"disambiguationData":[TD([[makeQuery(id+"F0.imprint","IMPRINT",EDGE,{"derivedFrom":subQ1}),1.0]])]});}
            var Q47;
            {var subQ0=sQuery(id+"F0.wireOp",EDGE,"E25.24.0");Q47=makeQuery(id+"F0.imprint","IMPRINT",FACE,{"disambiguationData":[TD([[makeQuery(id+"F0.imprint","IMPRINT",EDGE,{"derivedFrom":subQ0}),1.0]])]});}
            var Q48;
            {var subQ1=sQuery(id+"F0.wireOp",EDGE,"E25.23.0");Q48=makeQuery(id+"F0.imprint","IMPRINT",FACE,{"disambiguationData":[TD([[makeQuery(id+"F0.imprint","IMPRINT",EDGE,{"derivedFrom":subQ1}),1.0]])]});}
            var Q49;
            {var subQ0=sQuery(id+"F0.wireOp",EDGE,"E25.20.0");Q49=makeQuery(id+"F0.imprint","IMPRINT",FACE,{"disambiguationData":[TD([[makeQuery(id+"F0.imprint","IMPRINT",EDGE,{"derivedFrom":subQ0}),1.0]])]});}
            var Q50;
            {var subQ0=sQuery(id+"F0.wireOp",EDGE,"E25.19.0");Q50=makeQuery(id+"F0.imprint","IMPRINT",FACE,{"disambiguationData":[TD([[makeQuery(id+"F0.imprint","IMPRINT",EDGE,{"derivedFrom":subQ0}),1.0]])]});}
            var Q51;
            {var subQ1=sQuery(id+"F0.wireOp",EDGE,"E25.18.0");Q51=makeQuery(id+"F0.imprint","IMPRINT",FACE,{"disambiguationData":[TD([[makeQuery(id+"F0.imprint","IMPRINT",EDGE,{"derivedFrom":subQ1}),1.0]])]});}
            var Q52;
            {var subQ3=sQuery(id+"F0.wireOp",EDGE,"E25.17.0");Q52=makeQuery(id+"F0.imprint","IMPRINT",FACE,{"disambiguationData":[TD([[makeQuery(id+"F0.imprint","IMPRINT",EDGE,{"derivedFrom":subQ3}),1.0]])]});}
            var Q53;
            {var subQ3=sQuery(id+"F0.wireOp",EDGE,"E25.16.0");Q53=makeQuery(id+"F0.imprint","IMPRINT",FACE,{"disambiguationData":[TD([[makeQuery(id+"F0.imprint","IMPRINT",EDGE,{"derivedFrom":subQ3}),1.0]])]});}
            var Q54;
            {var subQ0=sQuery(id+"F0.wireOp",EDGE,"E25.15.0");Q54=makeQuery(id+"F0.imprint","IMPRINT",FACE,{"disambiguationData":[TD([[makeQuery(id+"F0.imprint","IMPRINT",EDGE,{"derivedFrom":subQ0}),1.0]])]});}
            var Q55;
            {var subQ0=sQuery(id+"F0.wireOp",EDGE,"E25.14.0");Q55=makeQuery(id+"F0.imprint","IMPRINT",FACE,{"disambiguationData":[TD([[makeQuery(id+"F0.imprint","IMPRINT",EDGE,{"derivedFrom":subQ0}),1.0]])]});}
            var Q56;
            {var subQ1=sQuery(id+"F0.wireOp",EDGE,"E25.13.0");Q56=makeQuery(id+"F0.imprint","IMPRINT",FACE,{"disambiguationData":[TD([[makeQuery(id+"F0.imprint","IMPRINT",EDGE,{"derivedFrom":subQ1}),1.0]])]});}
            var Q57;
            {var subQ3=sQuery(id+"F0.wireOp",EDGE,"E25.12.0");Q57=makeQuery(id+"F0.imprint","IMPRINT",FACE,{"disambiguationData":[TD([[makeQuery(id+"F0.imprint","IMPRINT",EDGE,{"derivedFrom":subQ3}),1.0]])]});}
            var Q58;
            {var subQ1=sQuery(id+"F0.wireOp",EDGE,"E25.11.0");Q58=makeQuery(id+"F0.imprint","IMPRINT",FACE,{"disambiguationData":[TD([[makeQuery(id+"F0.imprint","IMPRINT",EDGE,{"derivedFrom":subQ1}),1.0]])]});}
            var Q59;
            {var subQ0=sQuery(id+"F0.wireOp",EDGE,"E25.10.0");Q59=makeQuery(id+"F0.imprint","IMPRINT",FACE,{"disambiguationData":[TD([[makeQuery(id+"F0.imprint","IMPRINT",EDGE,{"derivedFrom":subQ0}),1.0]])]});}
            var Q60;
            {var subQ0=sQuery(id+"F0.wireOp",EDGE,"E25.9.0");Q60=makeQuery(id+"F0.imprint","IMPRINT",FACE,{"disambiguationData":[TD([[makeQuery(id+"F0.imprint","IMPRINT",EDGE,{"derivedFrom":subQ0}),1.0]])]});}
            var Q61;
            {var subQ1=sQuery(id+"F0.wireOp",EDGE,"E25.8.0");Q61=makeQuery(id+"F0.imprint","IMPRINT",FACE,{"disambiguationData":[TD([[makeQuery(id+"F0.imprint","IMPRINT",EDGE,{"derivedFrom":subQ1}),1.0]])]});}
            var Q62;
            {var subQ3=sQuery(id+"F0.wireOp",EDGE,"E25.7.0");Q62=makeQuery(id+"F0.imprint","IMPRINT",FACE,{"disambiguationData":[TD([[makeQuery(id+"F0.imprint","IMPRINT",EDGE,{"derivedFrom":subQ3}),1.0]])]});}
            var Q63;
            {var subQ1=sQuery(id+"F0.wireOp",EDGE,"E25.6.0");Q63=makeQuery(id+"F0.imprint","IMPRINT",FACE,{"disambiguationData":[TD([[makeQuery(id+"F0.imprint","IMPRINT",EDGE,{"derivedFrom":subQ1}),1.0]])]});}
            var Q64;
            {var subQ0=sQuery(id+"F0.wireOp",EDGE,"E25.5.0");Q64=makeQuery(id+"F0.imprint","IMPRINT",FACE,{"disambiguationData":[TD([[makeQuery(id+"F0.imprint","IMPRINT",EDGE,{"derivedFrom":subQ0}),1.0]])]});}
            var Q65;
            {var subQ0=sQuery(id+"F0.wireOp",EDGE,"E25.4.0");Q65=makeQuery(id+"F0.imprint","IMPRINT",FACE,{"disambiguationData":[TD([[makeQuery(id+"F0.imprint","IMPRINT",EDGE,{"derivedFrom":subQ0}),1.0]])]});}
            var Q66;
            {var subQ1=sQuery(id+"F0.wireOp",EDGE,"E25.3.0");Q66=makeQuery(id+"F0.imprint","IMPRINT",FACE,{"disambiguationData":[TD([[makeQuery(id+"F0.imprint","IMPRINT",EDGE,{"derivedFrom":subQ1}),1.0]])]});}
            var Q67;
            {var subQ3=sQuery(id+"F0.wireOp",EDGE,"E25.2.0");Q67=makeQuery(id+"F0.imprint","IMPRINT",FACE,{"disambiguationData":[TD([[makeQuery(id+"F0.imprint","IMPRINT",EDGE,{"derivedFrom":subQ3}),1.0]])]});}
            var Q68;
            {var subQ1=sQuery(id+"F0.wireOp",EDGE,"E25.1.0");Q68=makeQuery(id+"F0.imprint","IMPRINT",FACE,{"disambiguationData":[TD([[makeQuery(id+"F0.imprint","IMPRINT",EDGE,{"derivedFrom":subQ1}),1.0]])]});}
            var Q69;
            {var subQ0=sQuery(id+"F0.wireOp",EDGE,"E22");Q69=makeQuery(id+"F0.imprint","IMPRINT",FACE,{"disambiguationData":[TD([[makeQuery(id+"F0.imprint","IMPRINT",EDGE,{"derivedFrom":subQ0}),1.0]])]});}
            var Q70;
            {var subQ0=sQuery(id+"F0.wireOp",EDGE,"E19");Q70=makeQuery(id+"F0.imprint","IMPRINT",FACE,{"disambiguationData":[TD([[makeQuery(id+"F0.imprint","IMPRINT",EDGE,{"derivedFrom":subQ0}),-1.0]])]});}
            var Q71;
            {var subQ4=sQuery(id+"F0.wireOp",EDGE,"E19");Q71=makeQuery(id+"F0.imprint","IMPRINT",FACE,{"disambiguationData":[TD([[makeQuery(id+"F0.imprint","IMPRINT",EDGE,{"derivedFrom":subQ4}),1.0]])]});}
            var Q72;
            {var subQ4=sQuery(id+"F0.wireOp",EDGE,"E22");Q72=makeQuery(id+"F0.imprint","IMPRINT",FACE,{"disambiguationData":[TD([[makeQuery(id+"F0.imprint","IMPRINT",EDGE,{"derivedFrom":subQ4}),-1.0]])]});}
            var Q73;
            {var subQ0=sQuery(id+"F0.wireOp",EDGE,"E3");Q73=makeQuery(id+"F0.imprint","IMPRINT",FACE,{"disambiguationData":[TD([[makeQuery(id+"F0.imprint","IMPRINT",EDGE,{"derivedFrom":subQ0}),-1.0]])]});}
            extrude(context, id + "F1", {"entities" : qUnion([Q0, Q1, Q2, Q3, Q4, Q5, Q6, Q7, Q8, Q9, Q10, Q11, Q12, Q13, Q14, Q15, Q16, Q17, Q18, Q19, Q20, Q21, Q22, Q23, Q24, Q25, Q26, Q27, Q28, Q29, Q30, Q31, Q32, Q33, Q34, Q35, Q36, Q37, Q38, Q39, Q40, Q41, Q42, Q43, Q44, Q45, Q46, Q47, Q48, Q49, Q50, Q51, Q52, Q53, Q54, Q55, Q56, Q57, Q58, Q59, Q60, Q61, Q62, Q63, Q64, Q65, Q66, Q67, Q68, Q69, Q70, Q71, Q72, Q73]), "depth" : 13.97 * mm, "offsetDistance" : 25.4 * mm});
        }
    });
